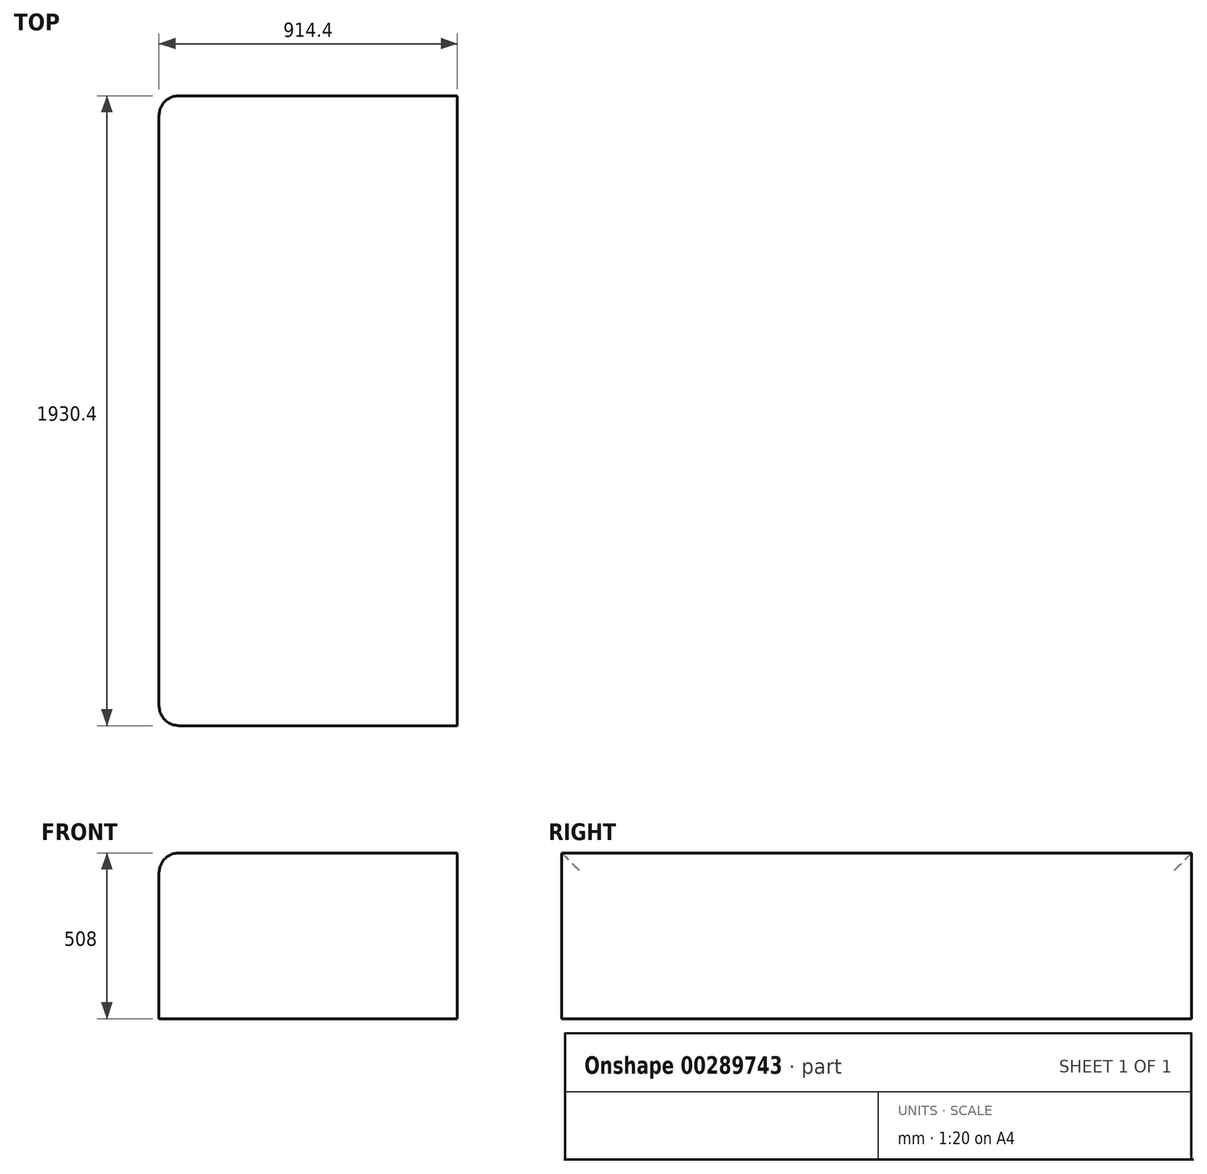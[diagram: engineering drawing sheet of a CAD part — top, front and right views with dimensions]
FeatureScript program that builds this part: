
annotation { "Feature Type Name" : "Feature", "Feature Type Description" : "" }
export const myFeature = defineFeature(function(context is Context, id is Id, definition is map)
    precondition{}
    {
        {
            var Q0;
            Q0=qCreatedBy(makeId("Front.planeOp"),FACE);
            var sketch = newSketch(context, id + "F0", { "sketchPlane" : qUnion([Q0])});
            skLineSegment(sketch, "E0.bottom", {"start": v(457.2, -254) * mm, "end": v(-457.2, -254) * mm});
            skLineSegment(sketch, "E0.top", {"start": v(457.2, 254) * mm, "end": v(-457.2, 254) * mm});
            skLineSegment(sketch, "E0.left", {"start": v(457.2, -254) * mm, "end": v(457.2, 254) * mm});
            skLineSegment(sketch, "E0.right", {"start": v(-457.2, -254) * mm, "end": v(-457.2, 254) * mm});
            skPoint(sketch, "E0.middle", {"position": v(0, 0) * mm});
            skSolve(sketch);
        }
        {
            var Q0;
            Q0=makeQuery(id+"F0.imprint","IMPRINT",FACE,{"disambiguationData":[TD([[makeQuery(id+"F0.imprint","IMPRINT",EDGE,{"derivedFrom":sQuery(id+"F0.wireOp",EDGE,"E0.bottom")}),-1.0]])]});
            extrude(context, id + "F1", {"entities" : qUnion([Q0]), "depth" : 1930.4 * mm, "offsetDistance" : 30.48 * mm});
        }
        {
            var Q0;
            Q0=makeQuery(id+"F1.opExtrude","SWEPT_EDGE",EDGE,{"disambiguationData":[OSD([sQuery(id+"F0.wireOp",EDGE,"E0.top"),sQuery(id+"F0.wireOp",EDGE,"E0.right")])]});
            var Q1;
            Q1=makeQuery(id+"F1.opExtrude","CAP_EDGE",EDGE,{"disambiguationData":[OSD([sQuery(id+"F0.wireOp",EDGE,"E0.right")])],"isStart":false});
            var Q2;
            Q2=makeQuery(id+"F1.opExtrude","CAP_EDGE",EDGE,{"disambiguationData":[OSD([sQuery(id+"F0.wireOp",EDGE,"E0.right")])],"isStart":true});
            fillet(context, id + "F2", {"entities" : qUnion([Q0, Q1, Q2]), "tangentPropagation" : true, "radius" : 60.96 * mm, "defaultsChanged" : true, "vertexSettings" : [], "allowEdgeOverflow" : false});
        }
    });
